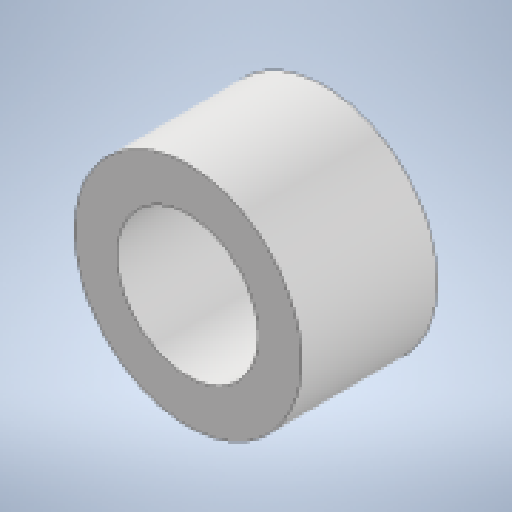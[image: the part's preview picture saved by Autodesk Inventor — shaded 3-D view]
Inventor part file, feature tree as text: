
AUTODESK INVENTOR PART (.ipt)
format: ipt  version: 2023 (Build 270158000, 158)  size: 140,288 bytes
history: native  units: in
note: dims shown in document units (in); Inventor stores cm internally (conversion verified against a paired STEP export)
features: extrude x1, sketch x1
ambient origin geometry x8: Origin, YZ Plane, XZ Plane, XY Plane, X Axis, Y Axis, Z Axis, Center Point
bodies: Solid1 (feature_tree)
feature tree (2):
  extrude  "Extrusion1"  Depth=0.3937in
  sketch  "Sketch1"  dims[d0=0.2441in d1=0.3937in d2=0.2362in d3=0.0in]
